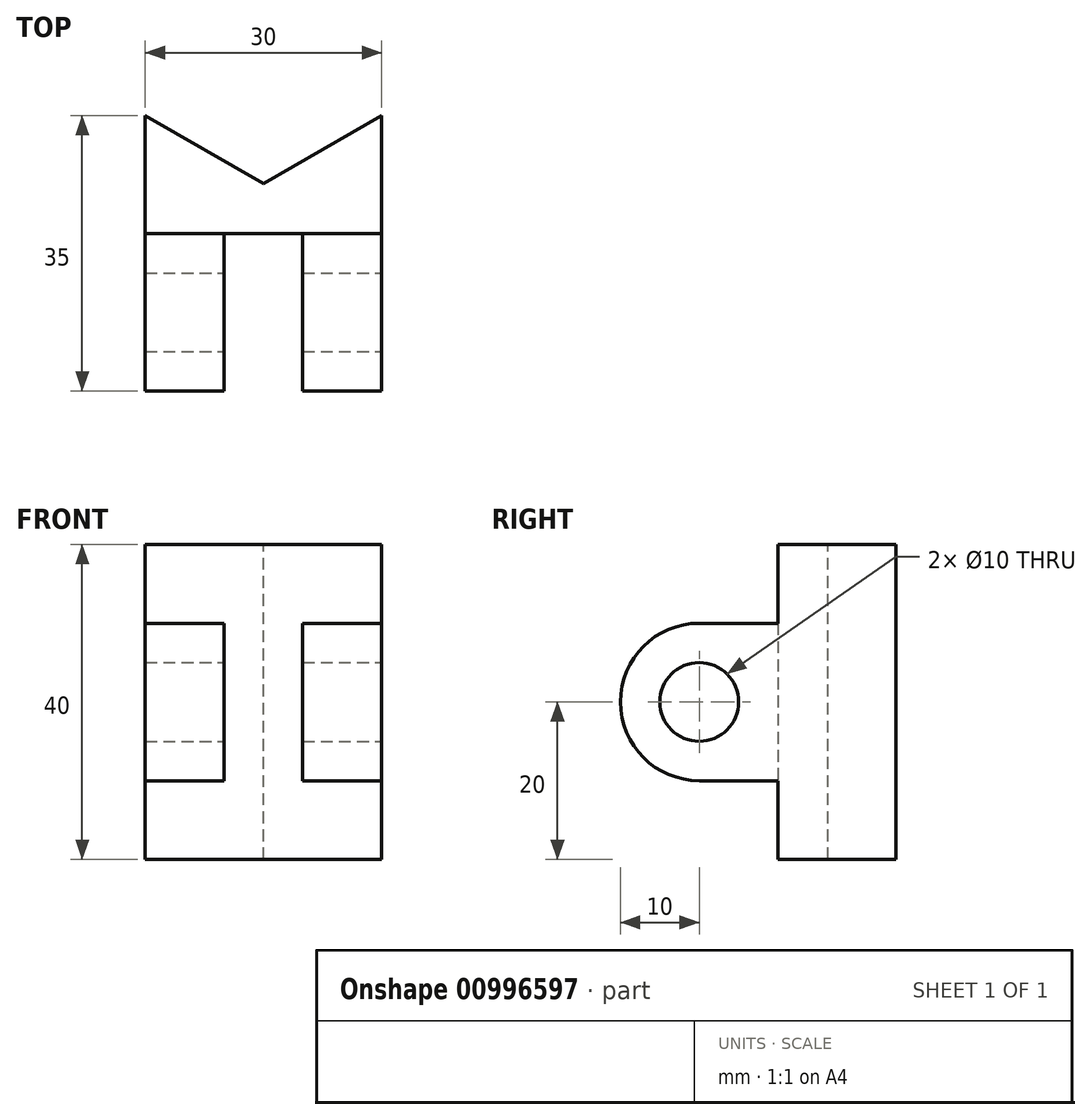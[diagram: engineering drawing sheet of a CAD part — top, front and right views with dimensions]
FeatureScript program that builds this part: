
annotation { "Feature Type Name" : "Feature", "Feature Type Description" : "" }
export const myFeature = defineFeature(function(context is Context, id is Id, definition is map)
    precondition{}
    {
        {
            var Q0;
            Q0=qCreatedBy(makeId("Front.planeOp"),FACE);
            var sketch = newSketch(context, id + "F0", { "sketchPlane" : qUnion([Q0])});
            skLineSegment(sketch, "E0.bottom", {"start": v(-15, 20) * mm, "end": v(15, 20) * mm});
            skLineSegment(sketch, "E0.top", {"start": v(-15, -20) * mm, "end": v(15, -20) * mm});
            skLineSegment(sketch, "E0.left", {"start": v(-15, 20) * mm, "end": v(-15, -20) * mm});
            skLineSegment(sketch, "E0.right", {"start": v(15, 20) * mm, "end": v(15, -20) * mm});
            skSolve(sketch);
        }
        {
            var Q0;
            Q0=makeQuery(id+"F0.imprint","IMPRINT",FACE,{"disambiguationData":[TD([[makeQuery(id+"F0.imprint","IMPRINT",EDGE,{"derivedFrom":sQuery(id+"F0.wireOp",EDGE,"E0.bottom")}),-1.0]])]});
            extrude(context, id + "F1", {"entities" : qUnion([Q0]), "depth" : 15 * mm, "offsetDistance" : 25 * mm});
        }
        {
            var Q0;
            Q0=makeQuery(id+"F1.opExtrude","CAP_FACE",FACE,{"disambiguationData":[OSD([sQuery(id+"F0.wireOp",EDGE,"E0.bottom"),sQuery(id+"F0.wireOp",EDGE,"E0.top"),sQuery(id+"F0.wireOp",EDGE,"E0.left"),sQuery(id+"F0.wireOp",EDGE,"E0.right")])],"isStart":false});
            var sketch = newSketch(context, id + "F2", { "sketchPlane" : qUnion([Q0])});
            skLineSegment(sketch, "E1.bottom", {"start": v(-15, 10) * mm, "end": v(-5, 10) * mm});
            skLineSegment(sketch, "E1.top", {"start": v(-15, -10) * mm, "end": v(-5, -10) * mm});
            skLineSegment(sketch, "E1.left", {"start": v(-15, 10) * mm, "end": v(-15, -10) * mm});
            skLineSegment(sketch, "E1.right", {"start": v(-5, 10) * mm, "end": v(-5, -10) * mm});
            skLineSegment(sketch, "E2.bottom", {"start": v(5, 10) * mm, "end": v(15, 10) * mm});
            skLineSegment(sketch, "E2.top", {"start": v(5, -10) * mm, "end": v(15, -10) * mm});
            skLineSegment(sketch, "E2.left", {"start": v(5, 10) * mm, "end": v(5, -10) * mm});
            skLineSegment(sketch, "E2.right", {"start": v(15, 10) * mm, "end": v(15, -10) * mm});
            skSolve(sketch);
        }
        {
            var Q0;
            Q0=makeQuery(id+"F2.imprint","IMPRINT",FACE,{"disambiguationData":[TD([[makeQuery(id+"F2.imprint","IMPRINT",EDGE,{"derivedFrom":sQuery(id+"F2.wireOp",EDGE,"E1.bottom")}),-1.0]])]});
            var Q1;
            Q1=makeQuery(id+"F2.imprint","IMPRINT",FACE,{"disambiguationData":[TD([[makeQuery(id+"F2.imprint","IMPRINT",EDGE,{"derivedFrom":sQuery(id+"F2.wireOp",EDGE,"E2.bottom")}),-1.0]])]});
            extrude(context, id + "F3", {"entities" : qUnion([Q0, Q1]), "operationType" : NewBodyOperationType.ADD, "depth" : 20 * mm, "offsetDistance" : 25 * mm});
        }
        {
            var Q0;
            Q0=makeQuery(id+"F3.boolean.opBoolean","MERGE",FACE,{"derivedFrom":[makeQuery(id+"F1.opExtrude","SWEPT_FACE",FACE,{"disambiguationData":[OSD([sQuery(id+"F0.wireOp",EDGE,"E0.right")])]}),makeQuery(id+"F3.opExtrude","SWEPT_FACE",FACE,{"disambiguationData":[OSD([sQuery(id+"F2.wireOp",EDGE,"E2.right")])]})]});
            var sketch = newSketch(context, id + "F4", { "sketchPlane" : qUnion([Q0])});
            skCircle(sketch, "E3", {"center": v(-25, 0) * mm, "radius": 5 * mm});
            skSolve(sketch);
        }
        {
            var Q0;
            Q0=makeQuery(id+"F4.imprint","IMPRINT",FACE,{"disambiguationData":[TD([[makeQuery(id+"F4.imprint","IMPRINT",EDGE,{"derivedFrom":sQuery(id+"F4.wireOp",EDGE,"E3")}),1.0]])]});
            extrude(context, id + "F5", {"entities" : qUnion([Q0]), "operationType" : NewBodyOperationType.REMOVE, "endBound" : BoundingType.THROUGH_ALL, "oppositeDirection" : true, "depth" : 25 * mm, "offsetDistance" : 25 * mm});
        }
        {
            var Q0;
            Q0=makeQuery(id+"F3.opExtrude","CAP_EDGE",EDGE,{"disambiguationData":[OSD([sQuery(id+"F2.wireOp",EDGE,"E2.bottom")])],"isStart":false});
            var Q1;
            Q1=makeQuery(id+"F3.opExtrude","CAP_EDGE",EDGE,{"disambiguationData":[OSD([sQuery(id+"F2.wireOp",EDGE,"E1.bottom")])],"isStart":false});
            var Q2;
            Q2=makeQuery(id+"F3.opExtrude","CAP_EDGE",EDGE,{"disambiguationData":[OSD([sQuery(id+"F2.wireOp",EDGE,"E1.top")])],"isStart":false});
            var Q3;
            Q3=makeQuery(id+"F3.opExtrude","CAP_EDGE",EDGE,{"disambiguationData":[OSD([sQuery(id+"F2.wireOp",EDGE,"E2.top")])],"isStart":false});
            fillet(context, id + "F6", {"entities" : qUnion([Q0, Q1, Q2, Q3]), "radius" : 10 * mm, "tangentPropagation" : true, "allowEdgeOverflow" : false});
        }
        {
            var Q0;
            Q0=makeQuery(id+"F1.opExtrude","SWEPT_FACE",FACE,{"disambiguationData":[OSD([sQuery(id+"F0.wireOp",EDGE,"E0.bottom")])]});
            var sketch = newSketch(context, id + "F7", { "sketchPlane" : qUnion([Q0])});
            skLineSegment(sketch, "E4", {"start": v(-15, 0) * mm, "end": v(0, -8.66) * mm});
            skLineSegment(sketch, "E5", {"start": v(0, -8.66) * mm, "end": v(15, 0) * mm});
            skSolve(sketch);
        }
        {
            var Q0;
            Q0=makeQuery(id+"F7.imprint","IMPRINT",FACE,{"disambiguationData":[TD([[makeQuery(id+"F7.imprint","IMPRINT",EDGE,{"derivedFrom":sQuery(id+"F7.wireOp",EDGE,"E4")}),1.0]])]});
            extrude(context, id + "F8", {"entities" : qUnion([Q0]), "operationType" : NewBodyOperationType.REMOVE, "endBound" : BoundingType.THROUGH_ALL, "oppositeDirection" : true, "depth" : 25 * mm, "offsetDistance" : 25 * mm});
        }
    });
